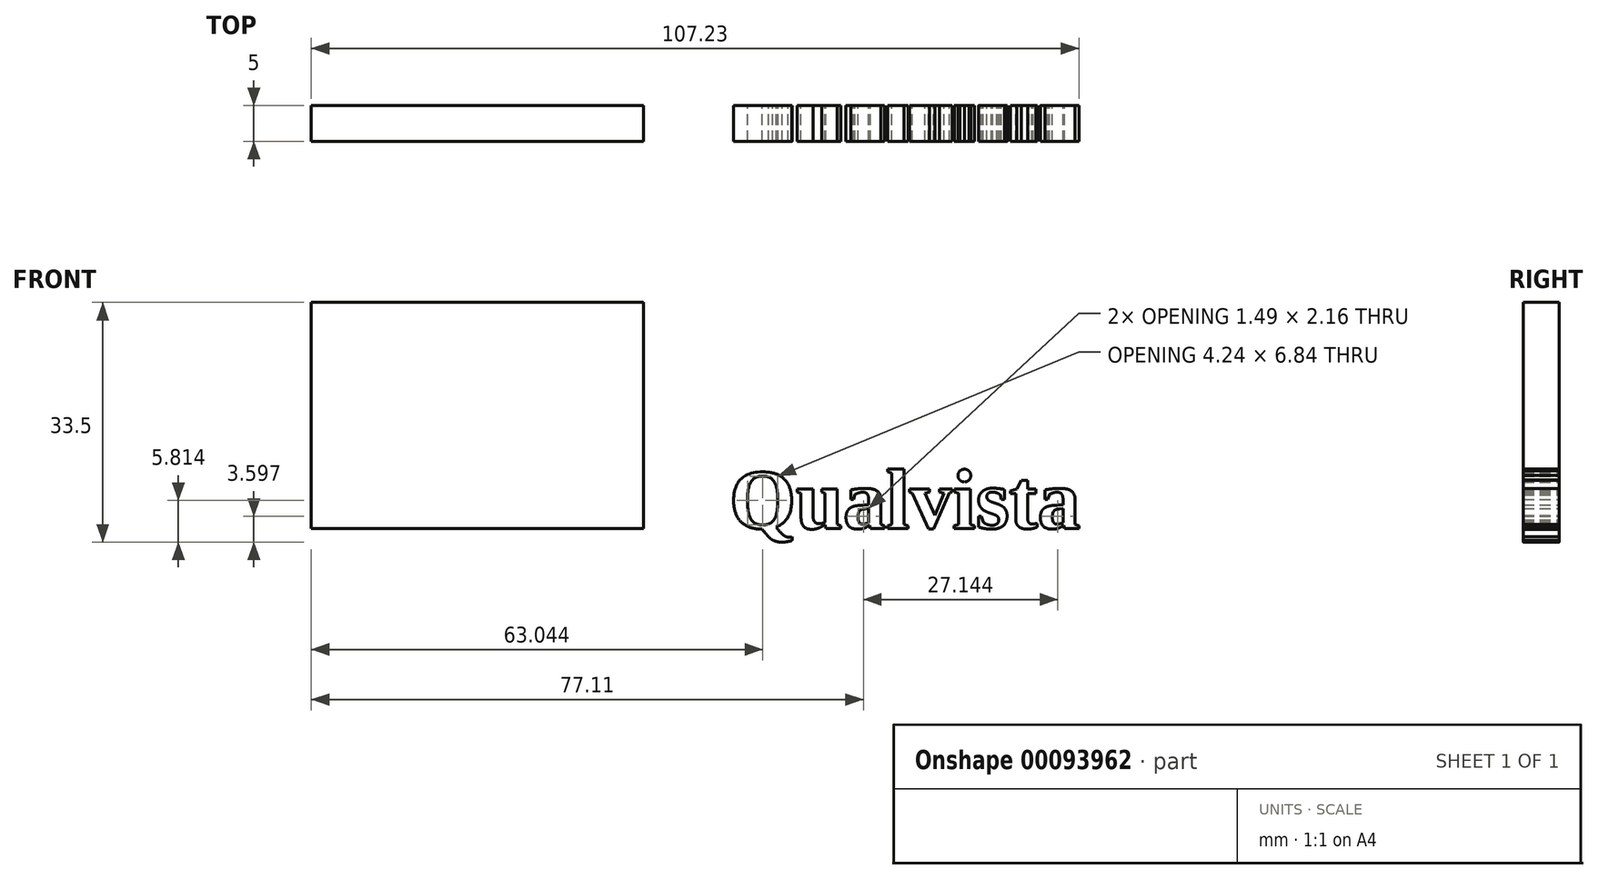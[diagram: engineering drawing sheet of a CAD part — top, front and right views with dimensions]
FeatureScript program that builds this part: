
annotation { "Feature Type Name" : "Feature", "Feature Type Description" : "" }
export const myFeature = defineFeature(function(context is Context, id is Id, definition is map)
    precondition{}
    {
        {
            var Q0;
            Q0=qCreatedBy(makeId("Front.planeOp"),FACE);
            var sketch = newSketch(context, id + "F0", { "sketchPlane" : qUnion([Q0])});
            skLineSegment(sketch, "E0.bottom", {"start": v(-46.38, 0) * mm, "end": v(0, 0) * mm});
            skLineSegment(sketch, "E0.top", {"start": v(-46.38, 31.57) * mm, "end": v(0, 31.57) * mm});
            skLineSegment(sketch, "E0.left", {"start": v(0, 31.57) * mm, "end": v(0, 0) * mm});
            skLineSegment(sketch, "E0.right", {"start": v(-46.38, 31.57) * mm, "end": v(-46.38, 0) * mm});
            skPoint(sketch, "E1", {"position": v(0, 31.57) * mm});
            skPoint(sketch, "E2", {"position": v(0.06, 31.57) * mm});
            skText(sketch, "E3", { "text": "Qualvista", "fontName": "Tinos-Bold.ttf"});
            const initialGuessF0  = {"E3": [0.01203, 0, 1, 0, 0.00858]};
            skSetInitialGuess(sketch, initialGuessF0);
            skSolve(sketch);
        }
        {
            var Q0;
            Q0 = qSketchRegion(id + "F0", true);
            extrude(context, id + "F1", {"entities" : qUnion([Q0]), "depth" : 5 * mm});
        }
    });
